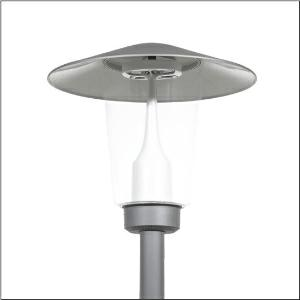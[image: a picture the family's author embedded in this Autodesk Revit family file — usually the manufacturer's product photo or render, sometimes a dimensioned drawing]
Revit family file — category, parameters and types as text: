
# Revit family: pilzleuchte_iq___p1_0a_5xa5235bf14hp_6096
name_source: partatom
category: Lighting Fixtures
units: mm (PartAtom-declared; Revit-internal decimal feet)

## family parameters
Cut with Voids When Loaded = No
Host = Face
Light Source = No
Part Type = Normal
Room Calculation Point = No
Round Connector Dimension = Use Diameter
Shared = No

## types (1)
- --- (1 x LED, 3920 lm, 33.6 W, 2200K)
    Apparent Load = 34 VA
    CIE Flux Codes = 35 64 90 96 100
    Color Rendering = 70
    Color Temperature = 2200K
    Default Elevation = 1800 mm
    Description = Mushroom Luminaire iQ, mast luminaire, Module 540 iQ-SR, primary light control with 3 zone facetted reflector, of plastic, silver coated, highly specular, structured, primary optical cover: cover, of PMMA, transparent, light distribution: P1.0a, light emission: direct distribution, primary light characteristic: strongly asymmetric, installation type: post-top, LED, High Power LED, rated luminous flux: 3.920lm, luminous efficacy: 117lm/W, light colour: 722, colour temperature: 2200K, control gear: ECG iQ, control: presetting dimming logarithmic, Street-Remote, Auto-Match, Temp-Guard, Lumen-Switch, Night-Set, Smart-Wire, Light-Fading, Desk-Remote (wireless, voltage-free reading and setting of iQ features in the workshop via application-optimized NFC function/RFID function), optimised constant luminous flux control (CLO 2.0), with terminal, 6-pole, max. 2.5mm², mains connection: 230..240V, AC, 50/60Hz, start of lifetime: 34W, end of service life: 36W, reduction: 15W, luminaire housing, upper part, of glass-fibre reinforced polyester, coated, Siteco® metallic grey (DB 702S), diameter: 650mm, height: 586mm, spigot size: d x l = 76 x 70mm (post-top) | with reducer (optional accessory) 60 x 70mm, post-top mast mounting element, of diecast aluminium, coated, Siteco® metallic grey (DB 702S), Module 540 iQ-SR, traffic white (RAL 9016), equipment: Power, protection rating (complete): IP65, insulation class (complete): insulation class II (safety insulation), certification: CE, ENEC, VDE, packaging unit: 1 piece

Light Distribution: P1.0a
    Height = 586 mm
    Lamp = 1 x LED
    Lamp Light Flux = 3920 lm
    Lamp Power = 33.6 W
    Lamp count = 1
    Length = 650 mm
    Luminous efficacy = 117 lm/W
    Manufacturer = Siteco
    ModVariant = No
    Model = 5XA5235BF14HP
    Number of Poles = 1
    OnlyDefault = Yes
    Power Factor = 1
    Product Name = Pilzleuchte iQ | P1.0a
    Product group = mast luminaire | pylon top
    ProductGroupID = 6100
    Protection Class = Protection class II
    Protection Degree = IP 65
    RLX_Detail_Level = 1
    RLX_Emergency_Light_Flux = 0 lm
    RLX_Emergency_Type = 0
    RLX_Emergency_Type_DB = No
    RlxData = <blob elided: 52429 chars, md5=8010839b>
    Socket = socket
    Standby Power = 0 W
    System Light Flux = 3920 lm
    System Power = 34 W
    Type Comments = factory setting: luminous flux: 100 % | dim-lin: 254 | 695 mA
    Type Image = l_1006077.jpg
    URL = http://relux.com
    VarID = @adj_144811
    Voltage = 0 V
    Weight = 0.00 kg
    Width = 0 mm  [stored 0 ft]

note: [stored X ft] marks values corroborated as IEEE doubles in the binary element streams (Revit-internal decimal feet)

## geometry (parser evidence)
native form markers: Blend x4, Sweep x11
no freeform markers — native parametric forms only
